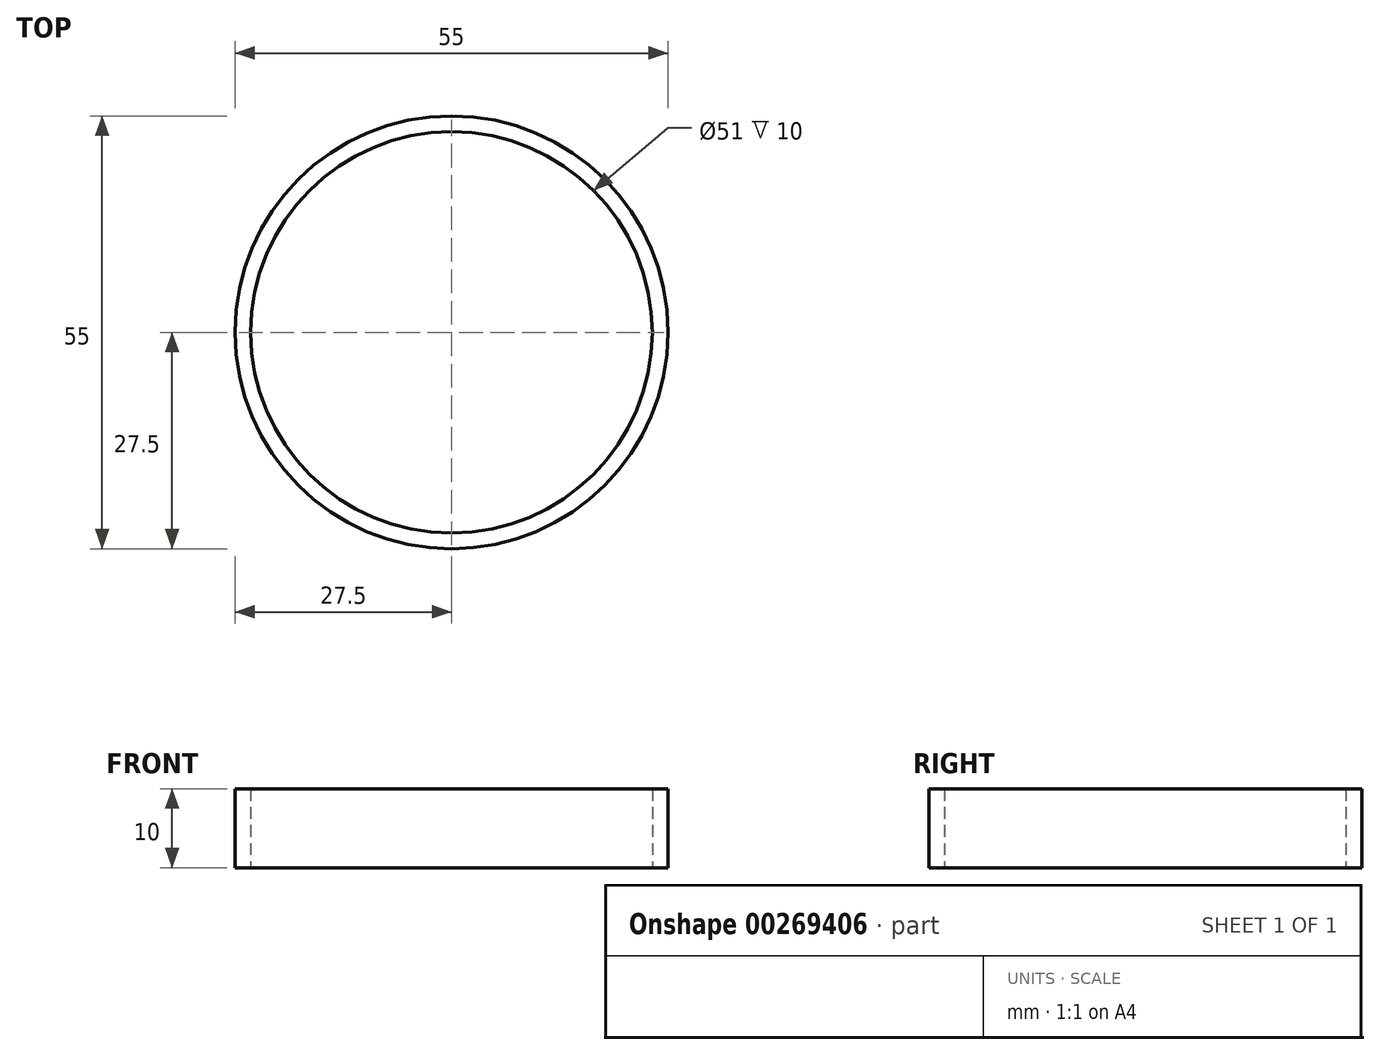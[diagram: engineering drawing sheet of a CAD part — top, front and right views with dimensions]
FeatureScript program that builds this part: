
annotation { "Feature Type Name" : "Feature", "Feature Type Description" : "" }
export const myFeature = defineFeature(function(context is Context, id is Id, definition is map)
    precondition{}
    {
        {
            var Q0;
            Q0=qCreatedBy(makeId("Top.planeOp"),FACE);
            var sketch = newSketch(context, id + "F0", { "sketchPlane" : qUnion([Q0])});
            skCircle(sketch, "E0", {"center": v(0, 0) * mm, "radius": 25.5 * mm});
            skCircle(sketch, "E1", {"center": v(0, 0) * mm, "radius": 27.5 * mm});
            skSolve(sketch);
        }
        {
            var Q0;
            Q0=makeQuery(id+"F0.imprint","IMPRINT",FACE,{"disambiguationData":[TD([[makeQuery(id+"F0.imprint","IMPRINT",EDGE,{"derivedFrom":sQuery(id+"F0.wireOp",EDGE,"E0")}),-1.0]])]});
            extrude(context, id + "F1", {"entities" : qUnion([Q0]), "depth" : 10 * mm});
        }
    });
